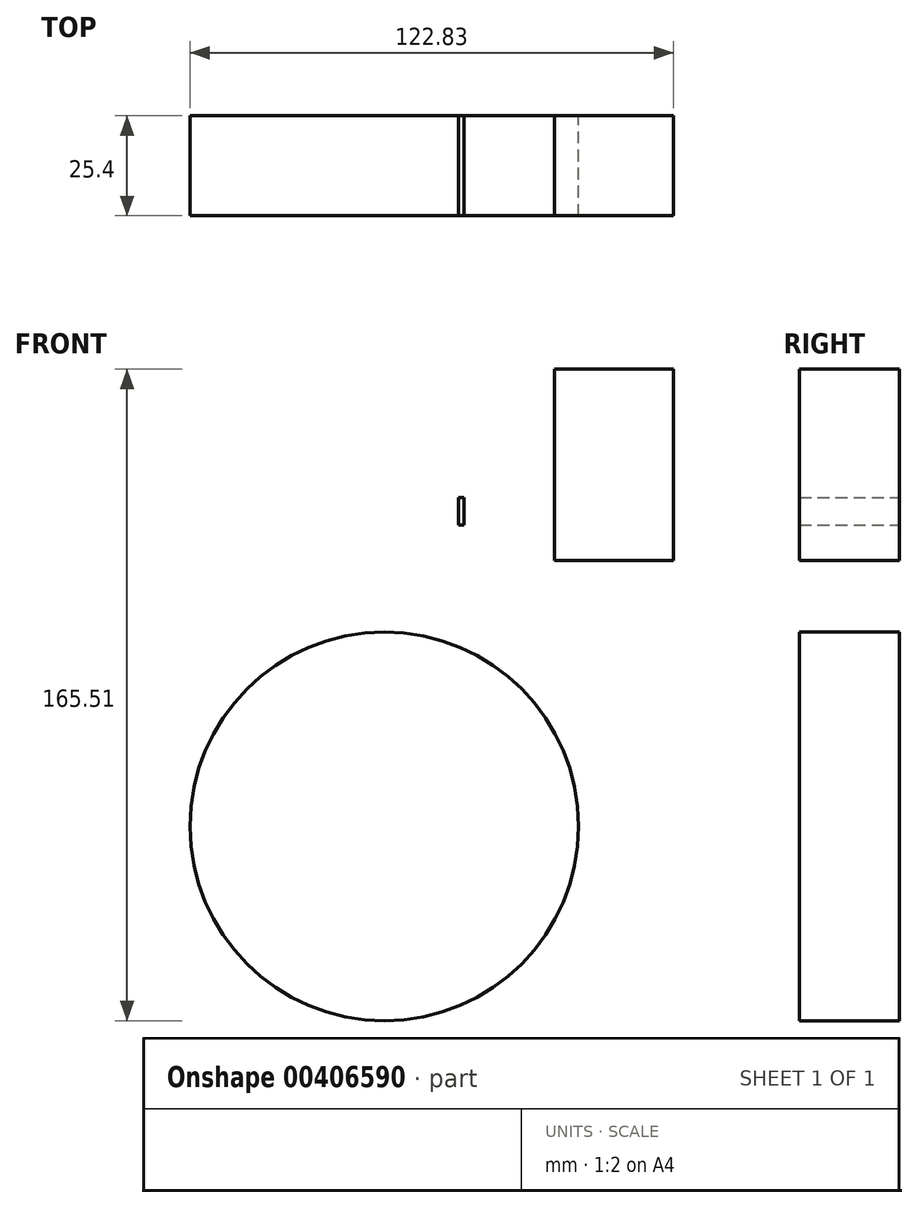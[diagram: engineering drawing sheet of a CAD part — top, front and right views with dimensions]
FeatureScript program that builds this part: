
annotation { "Feature Type Name" : "Feature", "Feature Type Description" : "" }
export const myFeature = defineFeature(function(context is Context, id is Id, definition is map)
    precondition{}
    {
        {
            var Q0;
            Q0=qCreatedBy(makeId("Front.planeOp"),FACE);
            var sketch = newSketch(context, id + "F0", { "sketchPlane" : qUnion([Q0])});
            skLineSegment(sketch, "E0.bottom", {"start": v(36.45, 0) * mm, "end": v(-35.09, 0) * mm});
            skLineSegment(sketch, "E0.top", {"start": v(36.45, 61.05) * mm, "end": v(-35.09, 61.05) * mm});
            skLineSegment(sketch, "E0.left", {"start": v(36.45, 0) * mm, "end": v(36.45, 61.05) * mm});
            skLineSegment(sketch, "E0.right", {"start": v(-35.09, 0) * mm, "end": v(-35.09, 61.05) * mm});
            skSolve(sketch);
        }
        {
            var Q0;
            Q0=makeQuery(id+"F0.imprint","IMPRINT",FACE,{"disambiguationData":[TD([[makeQuery(id+"F0.imprint","IMPRINT",EDGE,{"derivedFrom":sQuery(id+"F0.wireOp",EDGE,"E0.bottom")}),-1.0]])]});
            var sketch = newSketch(context, id + "F1", { "sketchPlane" : qUnion([Q0])});
            skLineSegment(sketch, "E1.bottom", {"start": v(20.24, 83.5) * mm, "end": v(18.79, 83.5) * mm});
            skLineSegment(sketch, "E1.top", {"start": v(20.24, 76.52) * mm, "end": v(18.79, 76.52) * mm});
            skLineSegment(sketch, "E1.left", {"start": v(20.24, 83.5) * mm, "end": v(20.24, 76.52) * mm});
            skLineSegment(sketch, "E1.right", {"start": v(18.79, 83.5) * mm, "end": v(18.79, 76.52) * mm});
            skLineSegment(sketch, "E2.bottom", {"start": v(43.28, 67.54) * mm, "end": v(73.46, 67.54) * mm});
            skLineSegment(sketch, "E2.top", {"start": v(43.28, 116.14) * mm, "end": v(73.46, 116.14) * mm});
            skLineSegment(sketch, "E2.left", {"start": v(43.28, 67.54) * mm, "end": v(43.28, 116.14) * mm});
            skLineSegment(sketch, "E2.right", {"start": v(73.46, 67.54) * mm, "end": v(73.46, 116.14) * mm});
            skCircle(sketch, "E3", {"center": v(0, 0) * mm, "radius": 49.37 * mm});
            skSolve(sketch);
        }
        {
            var Q0;
            Q0 = qSketchRegion(id + "F1", true);
            extrude(context, id + "F2", {"entities" : qUnion([Q0]), "depth" : 25.4 * mm});
        }
    });
